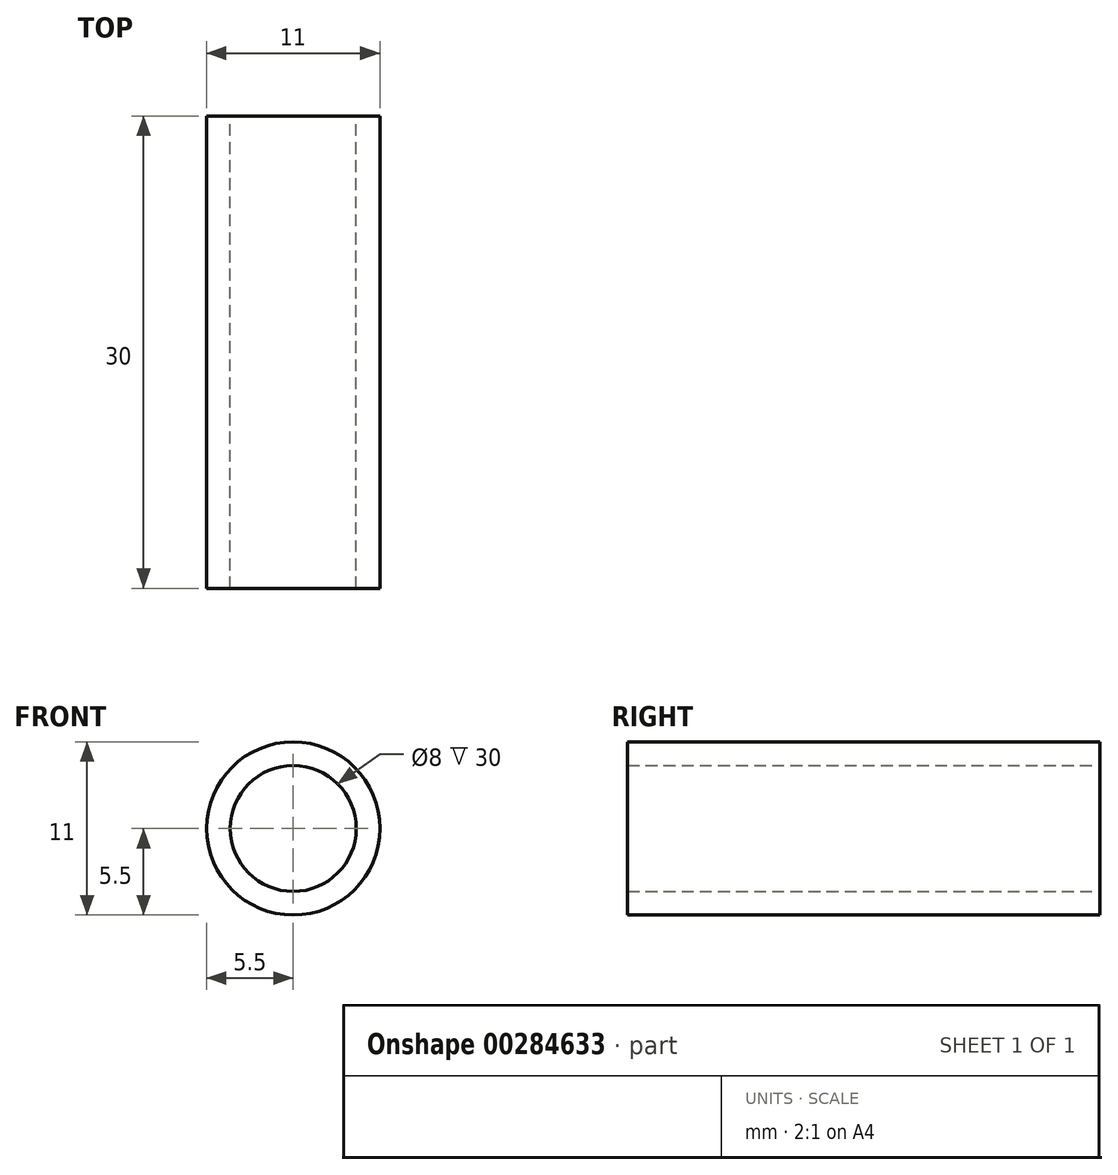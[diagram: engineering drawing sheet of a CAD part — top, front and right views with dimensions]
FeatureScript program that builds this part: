
annotation { "Feature Type Name" : "Feature", "Feature Type Description" : "" }
export const myFeature = defineFeature(function(context is Context, id is Id, definition is map)
    precondition{}
    {
        {
            var Q0;
            Q0=qCreatedBy(makeId("Front.planeOp"),FACE);
            var sketch = newSketch(context, id + "F0", { "sketchPlane" : qUnion([Q0])});
            skCircle(sketch, "E0", {"center": v(0, 0) * mm, "radius": 4 * mm});
            skCircle(sketch, "E1", {"center": v(0, 0) * mm, "radius": 5.5 * mm});
            skSolve(sketch);
        }
        {
            var Q0;
            Q0 = qSketchRegion(id + "F0", true);
            extrude(context, id + "F1", {"entities" : qUnion([Q0]), "depth" : 30 * mm, "symmetric" : true});
        }
    });
